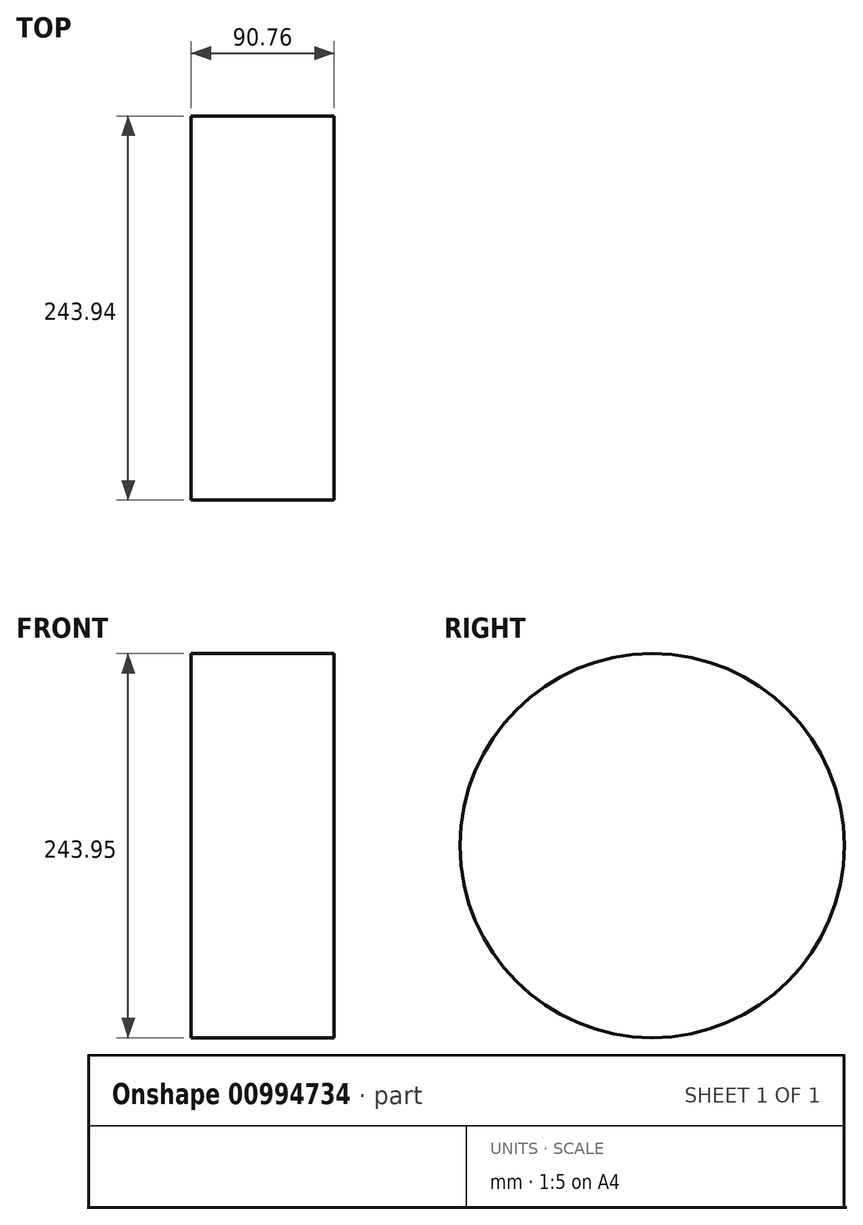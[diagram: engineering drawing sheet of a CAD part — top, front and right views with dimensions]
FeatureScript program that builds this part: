
annotation { "Feature Type Name" : "Feature", "Feature Type Description" : "" }
export const myFeature = defineFeature(function(context is Context, id is Id, definition is map)
    precondition{}
    {
        {
            var Q0;
            Q0=qCreatedBy(makeId("Right.planeOp"),FACE);
            var sketch = newSketch(context, id + "F0", { "sketchPlane" : qUnion([Q0])});
            skCircle(sketch, "E0", {"center": v(0, 88.62) * mm, "radius": 121.97 * mm});
            skSolve(sketch);
        }
        {
            var Q0;
            Q0 = qSketchRegion(id + "F0", true);
            extrude(context, id + "F1", {"entities" : qUnion([Q0]), "depth" : 90.76 * mm, "offsetDistance" : 25.4 * mm});
        }
        {
            var Q0;
            Q0=makeQuery(id+"F1.opExtrude","CAP_FACE",FACE,{"disambiguationData":[OSD([sQuery(id+"F0.wireOp",EDGE,"E0")])],"isStart":false});
            var sketch = newSketch(context, id + "F2", { "sketchPlane" : qUnion([Q0])});
            skLineSegment(sketch, "E1.bottom", {"start": v(-0.17, 105.5) * mm, "end": v(-95.24, 105.5) * mm});
            skLineSegment(sketch, "E1.top", {"start": v(-0.17, 37.49) * mm, "end": v(-95.24, 37.49) * mm});
            skLineSegment(sketch, "E1.right", {"start": v(-95.24, 105.5) * mm, "end": v(-95.24, 37.49) * mm});
            skSolve(sketch);
        }
        {
            var Q0;
            Q0 = qBodyType(qCreatedBy(id + "F2" ,EDGE), BodyType.WIRE);
            var Q1;
            Q1=sQuery(id+"F2.wireOp",EDGE,"E1.bottom");
            extrude(context, id + "F3", {"bodyType" : ToolBodyType.SURFACE, "surfaceEntities" : qUnion([Q0, Q1]), "depth" : 176.07 * mm, "offsetDistance" : 25.4 * mm});
        }
    });
